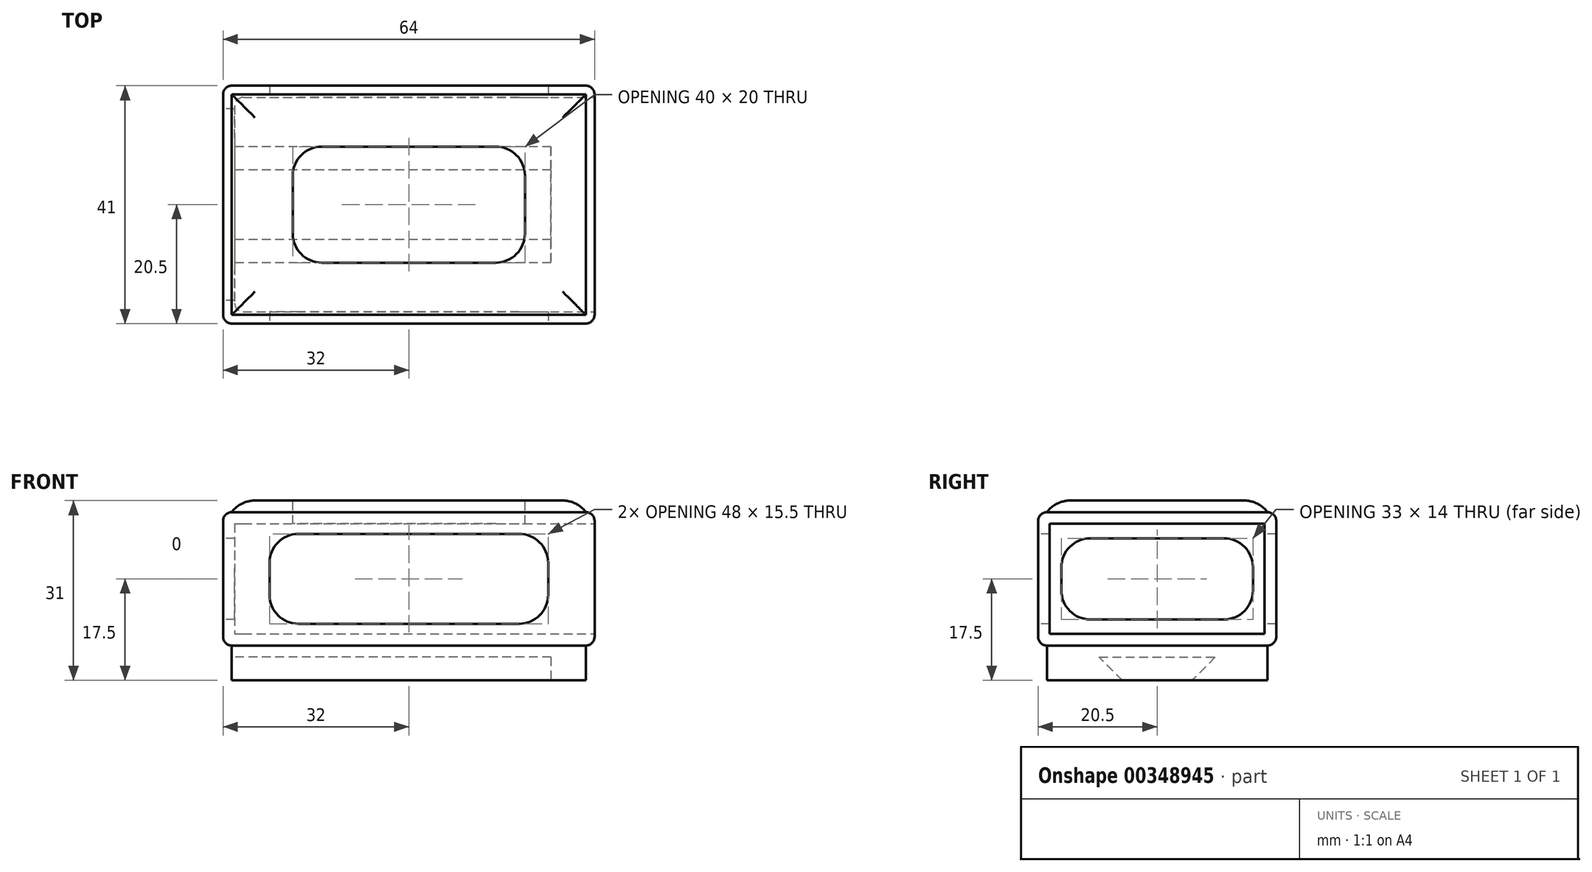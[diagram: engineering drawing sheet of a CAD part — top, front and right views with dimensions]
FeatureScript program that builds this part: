
annotation { "Feature Type Name" : "Feature", "Feature Type Description" : "" }
export const myFeature = defineFeature(function(context is Context, id is Id, definition is map)
    precondition{}
    {
        {
            var Q0;
            Q0=qCreatedBy(makeId("Top.planeOp"),FACE);
            var sketch = newSketch(context, id + "F0", { "sketchPlane" : qUnion([Q0])});
            skLineSegment(sketch, "E0.bottom", {"start": v(32, 20.5) * mm, "end": v(-32, 20.5) * mm});
            skLineSegment(sketch, "E0.top", {"start": v(32, -20.5) * mm, "end": v(-32, -20.5) * mm});
            skLineSegment(sketch, "E0.left", {"start": v(32, 20.5) * mm, "end": v(32, -20.5) * mm});
            skLineSegment(sketch, "E0.right", {"start": v(-32, 20.5) * mm, "end": v(-32, -20.5) * mm});
            skPoint(sketch, "E0.middle", {"position": v(0, 0) * mm});
            skSolve(sketch);
        }
        {
            var Q0;
            Q0=makeQuery(id+"F0.imprint","IMPRINT",FACE,{"disambiguationData":[TD([[makeQuery(id+"F0.imprint","IMPRINT",EDGE,{"derivedFrom":sQuery(id+"F0.wireOp",EDGE,"E0.bottom")}),1.0]])]});
            extrude(context, id + "F1", {"entities" : qUnion([Q0]), "depth" : 11.5 * mm});
        }
        {
            var Q0;
            Q0=makeQuery(id+"F1.opExtrude","CAP_EDGE",EDGE,{"disambiguationData":[OSD([sQuery(id+"F0.wireOp",EDGE,"E0.right")])],"isStart":false});
            var Q1;
            Q1=makeQuery(id+"F1.opExtrude","CAP_EDGE",EDGE,{"disambiguationData":[OSD([sQuery(id+"F0.wireOp",EDGE,"E0.top")])],"isStart":false});
            var Q2;
            Q2=makeQuery(id+"F1.opExtrude","CAP_EDGE",EDGE,{"disambiguationData":[OSD([sQuery(id+"F0.wireOp",EDGE,"E0.left")])],"isStart":false});
            var Q3;
            Q3=makeQuery(id+"F1.opExtrude","CAP_EDGE",EDGE,{"disambiguationData":[OSD([sQuery(id+"F0.wireOp",EDGE,"E0.bottom")])],"isStart":false});
            var Q4;
            Q4=makeQuery(id+"F1.opExtrude","SWEPT_EDGE",EDGE,{"disambiguationData":[OSD([sQuery(id+"F0.wireOp",EDGE,"E0.top"),sQuery(id+"F0.wireOp",EDGE,"E0.left")])]});
            var Q5;
            Q5=makeQuery(id+"F1.opExtrude","SWEPT_EDGE",EDGE,{"disambiguationData":[OSD([sQuery(id+"F0.wireOp",EDGE,"E0.bottom"),sQuery(id+"F0.wireOp",EDGE,"E0.left")])]});
            var Q6;
            Q6=makeQuery(id+"F1.opExtrude","SWEPT_EDGE",EDGE,{"disambiguationData":[OSD([sQuery(id+"F0.wireOp",EDGE,"E0.top"),sQuery(id+"F0.wireOp",EDGE,"E0.right")])]});
            var Q7;
            Q7=makeQuery(id+"F1.opExtrude","SWEPT_EDGE",EDGE,{"disambiguationData":[OSD([sQuery(id+"F0.wireOp",EDGE,"E0.bottom"),sQuery(id+"F0.wireOp",EDGE,"E0.right")])]});
            fillet(context, id + "F2", {"entities" : qUnion([Q0, Q1, Q2, Q3, Q4, Q5, Q6, Q7]), "radius" : 1.5 * mm, "tangentPropagation" : true, "allowEdgeOverflow" : false});
        }
        {
            var Q0;
            Q0=makeQuery(id+"F1.opExtrude","CAP_FACE",FACE,{"disambiguationData":[OSD([sQuery(id+"F0.wireOp",EDGE,"E0.bottom"),sQuery(id+"F0.wireOp",EDGE,"E0.top"),sQuery(id+"F0.wireOp",EDGE,"E0.left"),sQuery(id+"F0.wireOp",EDGE,"E0.right")])],"isStart":true});
            shell(context, id + "F3", {"entities" : qUnion([Q0]), "thickness" : 2 * mm});
        }
        {
            var Q0;
            Q0=makeQuery(id+"F3.opShell","OFFSET_EDGE",EDGE,{"disambiguationData":[OSD([sQuery(id+"F0.wireOp",EDGE,"E0.bottom"),sQuery(id+"F0.wireOp",EDGE,"E0.right")])]});
            var Q1;
            Q1=makeQuery(id+"F3.opShell","OFFSET_EDGE",EDGE,{"disambiguationData":[OSD([sQuery(id+"F0.wireOp",EDGE,"E0.top"),sQuery(id+"F0.wireOp",EDGE,"E0.right")])]});
            fillet(context, id + "F4", {"entities" : qUnion([Q0, Q1]), "radius" : 1.5 * mm, "tangentPropagation" : true, "allowEdgeOverflow" : false});
        }
        {
            var Q0;
            Q0=makeQuery(id+"F1.opExtrude","SWEPT_BODY",BODY,{"disambiguationData":[OSD([sQuery(id+"F0.wireOp",EDGE,"E0.bottom"),sQuery(id+"F0.wireOp",EDGE,"E0.top"),sQuery(id+"F0.wireOp",EDGE,"E0.left"),sQuery(id+"F0.wireOp",EDGE,"E0.right")])]});
            var Q1;
            Q1=qCreatedBy(makeId("Top.planeOp"),FACE);
            mirror(context, id + "F5", {"operationType" : NewBodyOperationType.ADD, "entities" : qUnion([Q0]), "mirrorPlane" : qUnion([Q1])});
        }
        {
            var Q0;
            {var subQ0=makeQuery(id+"F1.opExtrude","SWEPT_FACE",FACE,{"disambiguationData":[OSD([sQuery(id+"F0.wireOp",EDGE,"E0.top")])]});Q0=makeQuery(id+"F5.boolean.opBoolean","MERGE",FACE,{"derivedFrom":[subQ0,makeQuery(id+"F5.opPattern","COPY",FACE,{"derivedFrom":subQ0,"instanceName":"1"})]});}
            var sketch = newSketch(context, id + "F6", { "sketchPlane" : qUnion([Q0])});
            skLineSegment(sketch, "E1.bottom", {"start": v(24, -7.75) * mm, "end": v(-24, -7.75) * mm});
            skLineSegment(sketch, "E1.top", {"start": v(24, 7.75) * mm, "end": v(-24, 7.75) * mm});
            skLineSegment(sketch, "E1.left", {"start": v(24, -7.75) * mm, "end": v(24, 7.75) * mm});
            skLineSegment(sketch, "E1.right", {"start": v(-24, -7.75) * mm, "end": v(-24, 7.75) * mm});
            skPoint(sketch, "E1.middle", {"position": v(0, 0) * mm});
            skSolve(sketch);
        }
        {
            var Q0;
            Q0=makeQuery(id+"F6.imprint","IMPRINT",FACE,{"disambiguationData":[TD([[makeQuery(id+"F6.imprint","IMPRINT",EDGE,{"derivedFrom":sQuery(id+"F6.wireOp",EDGE,"E1.bottom")}),-1.0]])]});
            extrude(context, id + "F7", {"entities" : qUnion([Q0]), "operationType" : NewBodyOperationType.REMOVE, "endBound" : BoundingType.THROUGH_ALL, "oppositeDirection" : true, "depth" : 5 * mm});
        }
        {
            var Q0;
            {var subQ0=makeQuery(id+"F1.opExtrude","SWEPT_FACE",FACE,{"disambiguationData":[OSD([sQuery(id+"F0.wireOp",EDGE,"E0.right")])]});Q0=makeQuery(id+"F5.boolean.opBoolean","MERGE",FACE,{"derivedFrom":[subQ0,makeQuery(id+"F5.opPattern","COPY",FACE,{"derivedFrom":subQ0,"instanceName":"1"})]});}
            var sketch = newSketch(context, id + "F8", { "sketchPlane" : qUnion([Q0])});
            skLineSegment(sketch, "E2.bottom", {"start": v(16.5, 7) * mm, "end": v(-16.5, 7) * mm});
            skLineSegment(sketch, "E2.top", {"start": v(16.5, -7) * mm, "end": v(-16.5, -7) * mm});
            skLineSegment(sketch, "E2.left", {"start": v(16.5, 7) * mm, "end": v(16.5, -7) * mm});
            skLineSegment(sketch, "E2.right", {"start": v(-16.5, 7) * mm, "end": v(-16.5, -7) * mm});
            skPoint(sketch, "E2.middle", {"position": v(0, 0) * mm});
            skSolve(sketch);
        }
        {
            var Q0;
            Q0=makeQuery(id+"F8.imprint","IMPRINT",FACE,{"disambiguationData":[TD([[makeQuery(id+"F8.imprint","IMPRINT",EDGE,{"derivedFrom":sQuery(id+"F8.wireOp",EDGE,"E2.bottom")}),1.0]])]});
            extrude(context, id + "F9", {"entities" : qUnion([Q0]), "operationType" : NewBodyOperationType.REMOVE, "oppositeDirection" : true, "depth" : 5 * mm});
        }
        {
            var Q0;
            {var subQ0=sQuery(id+"F0.wireOp",EDGE,"E0.left");var subQ2=makeQuery(id+"F1.opExtrude","SWEPT_FACE",FACE,{"disambiguationData":[OSD([subQ0])]});var subQ3=sQuery(id+"F8.wireOp",EDGE,"E2.right");var subQ4=sQuery(id+"F8.wireOp",EDGE,"E2.top");Q0=makeQuery(id+"F9.boolean.opBoolean","COPY",EDGE,{"disambiguationData":[TD([subQ2])],"derivedFrom":makeQuery(id+"F9.opExtrude","SWEPT_EDGE",EDGE,{"disambiguationData":[OSD([subQ4,subQ3])]})});}
            var Q1;
            {var subQ0=sQuery(id+"F0.wireOp",EDGE,"E0.right");var subQ2=makeQuery(id+"F1.opExtrude","SWEPT_FACE",FACE,{"disambiguationData":[OSD([subQ0])]});var subQ3=sQuery(id+"F8.wireOp",EDGE,"E2.top");var subQ4=sQuery(id+"F8.wireOp",EDGE,"E2.right");Q1=makeQuery(id+"F9.boolean.opBoolean","COPY",EDGE,{"disambiguationData":[TD([subQ2])],"derivedFrom":makeQuery(id+"F9.opExtrude","SWEPT_EDGE",EDGE,{"disambiguationData":[OSD([subQ3,subQ4])]})});}
            var Q2;
            {var subQ0=sQuery(id+"F0.wireOp",EDGE,"E0.left");var subQ2=makeQuery(id+"F1.opExtrude","SWEPT_FACE",FACE,{"disambiguationData":[OSD([subQ0])]});var subQ3=sQuery(id+"F8.wireOp",EDGE,"E2.top");var subQ4=sQuery(id+"F8.wireOp",EDGE,"E2.left");Q2=makeQuery(id+"F9.boolean.opBoolean","COPY",EDGE,{"disambiguationData":[TD([subQ2])],"derivedFrom":makeQuery(id+"F9.opExtrude","SWEPT_EDGE",EDGE,{"disambiguationData":[OSD([subQ3,subQ4])]})});}
            var Q3;
            {var subQ0=sQuery(id+"F0.wireOp",EDGE,"E0.right");var subQ2=makeQuery(id+"F1.opExtrude","SWEPT_FACE",FACE,{"disambiguationData":[OSD([subQ0])]});var subQ3=sQuery(id+"F8.wireOp",EDGE,"E2.top");var subQ4=sQuery(id+"F8.wireOp",EDGE,"E2.left");Q3=makeQuery(id+"F9.boolean.opBoolean","COPY",EDGE,{"disambiguationData":[TD([subQ2])],"derivedFrom":makeQuery(id+"F9.opExtrude","SWEPT_EDGE",EDGE,{"disambiguationData":[OSD([subQ3,subQ4])]})});}
            var Q4;
            {var subQ0=sQuery(id+"F0.wireOp",EDGE,"E0.left");var subQ2=makeQuery(id+"F1.opExtrude","SWEPT_FACE",FACE,{"disambiguationData":[OSD([subQ0])]});var subQ3=sQuery(id+"F8.wireOp",EDGE,"E2.right");var subQ4=sQuery(id+"F8.wireOp",EDGE,"E2.bottom");Q4=makeQuery(id+"F9.boolean.opBoolean","COPY",EDGE,{"disambiguationData":[TD([subQ2])],"derivedFrom":makeQuery(id+"F9.opExtrude","SWEPT_EDGE",EDGE,{"disambiguationData":[OSD([subQ4,subQ3])]})});}
            var Q5;
            {var subQ0=sQuery(id+"F0.wireOp",EDGE,"E0.right");var subQ2=makeQuery(id+"F1.opExtrude","SWEPT_FACE",FACE,{"disambiguationData":[OSD([subQ0])]});var subQ3=sQuery(id+"F8.wireOp",EDGE,"E2.bottom");var subQ4=sQuery(id+"F8.wireOp",EDGE,"E2.right");Q5=makeQuery(id+"F9.boolean.opBoolean","COPY",EDGE,{"disambiguationData":[TD([subQ2])],"derivedFrom":makeQuery(id+"F9.opExtrude","SWEPT_EDGE",EDGE,{"disambiguationData":[OSD([subQ3,subQ4])]})});}
            var Q6;
            {var subQ0=sQuery(id+"F0.wireOp",EDGE,"E0.right");var subQ2=sQuery(id+"F8.wireOp",EDGE,"E2.bottom");var subQ3=makeQuery(id+"F1.opExtrude","SWEPT_FACE",FACE,{"disambiguationData":[OSD([subQ0])]});var subQ4=sQuery(id+"F8.wireOp",EDGE,"E2.left");Q6=makeQuery(id+"F9.boolean.opBoolean","COPY",EDGE,{"disambiguationData":[TD([subQ3])],"derivedFrom":makeQuery(id+"F9.opExtrude","SWEPT_EDGE",EDGE,{"disambiguationData":[OSD([subQ2,subQ4])]})});}
            var Q7;
            {var subQ0=sQuery(id+"F0.wireOp",EDGE,"E0.left");var subQ2=makeQuery(id+"F1.opExtrude","SWEPT_FACE",FACE,{"disambiguationData":[OSD([subQ0])]});var subQ3=sQuery(id+"F8.wireOp",EDGE,"E2.bottom");var subQ4=sQuery(id+"F8.wireOp",EDGE,"E2.left");Q7=makeQuery(id+"F9.boolean.opBoolean","COPY",EDGE,{"disambiguationData":[TD([subQ2])],"derivedFrom":makeQuery(id+"F9.opExtrude","SWEPT_EDGE",EDGE,{"disambiguationData":[OSD([subQ3,subQ4])]})});}
            fillet(context, id + "F10", {"entities" : qUnion([Q0, Q1, Q2, Q3, Q4, Q5, Q6, Q7]), "radius" : 5 * mm, "tangentPropagation" : true, "allowEdgeOverflow" : false});
        }
        {
            var Q0;
            {var subQ0=sQuery(id+"F0.wireOp",EDGE,"E0.top");var subQ2=makeQuery(id+"F1.opExtrude","SWEPT_FACE",FACE,{"disambiguationData":[OSD([subQ0])]});var subQ3=sQuery(id+"F6.wireOp",EDGE,"E1.top");var subQ4=sQuery(id+"F6.wireOp",EDGE,"E1.right");Q0=makeQuery(id+"F7.boolean.opBoolean","COPY",EDGE,{"disambiguationData":[TD([subQ2])],"derivedFrom":makeQuery(id+"F7.opExtrude","SWEPT_EDGE",EDGE,{"disambiguationData":[OSD([subQ3,subQ4])]})});}
            var Q1;
            {var subQ0=sQuery(id+"F0.wireOp",EDGE,"E0.top");var subQ2=makeQuery(id+"F1.opExtrude","SWEPT_FACE",FACE,{"disambiguationData":[OSD([subQ0])]});var subQ3=sQuery(id+"F6.wireOp",EDGE,"E1.left");var subQ4=sQuery(id+"F6.wireOp",EDGE,"E1.top");Q1=makeQuery(id+"F7.boolean.opBoolean","COPY",EDGE,{"disambiguationData":[TD([subQ2])],"derivedFrom":makeQuery(id+"F7.opExtrude","SWEPT_EDGE",EDGE,{"disambiguationData":[OSD([subQ4,subQ3])]})});}
            var Q2;
            {var subQ0=sQuery(id+"F0.wireOp",EDGE,"E0.top");var subQ2=sQuery(id+"F6.wireOp",EDGE,"E1.bottom");var subQ3=makeQuery(id+"F1.opExtrude","SWEPT_FACE",FACE,{"disambiguationData":[OSD([subQ0])]});var subQ4=sQuery(id+"F6.wireOp",EDGE,"E1.right");Q2=makeQuery(id+"F7.boolean.opBoolean","COPY",EDGE,{"disambiguationData":[TD([subQ3])],"derivedFrom":makeQuery(id+"F7.opExtrude","SWEPT_EDGE",EDGE,{"disambiguationData":[OSD([subQ2,subQ4])]})});}
            var Q3;
            {var subQ0=sQuery(id+"F0.wireOp",EDGE,"E0.top");var subQ2=sQuery(id+"F6.wireOp",EDGE,"E1.bottom");var subQ3=makeQuery(id+"F1.opExtrude","SWEPT_FACE",FACE,{"disambiguationData":[OSD([subQ0])]});var subQ4=sQuery(id+"F6.wireOp",EDGE,"E1.left");Q3=makeQuery(id+"F7.boolean.opBoolean","COPY",EDGE,{"disambiguationData":[TD([subQ3])],"derivedFrom":makeQuery(id+"F7.opExtrude","SWEPT_EDGE",EDGE,{"disambiguationData":[OSD([subQ2,subQ4])]})});}
            fillet(context, id + "F11", {"entities" : qUnion([Q0, Q1, Q2, Q3]), "radius" : 5 * mm, "tangentPropagation" : true, "allowEdgeOverflow" : false});
        }
        {
            var Q0;
            {var subQ0=sQuery(id+"F0.wireOp",EDGE,"E0.bottom");var subQ1=makeQuery(id+"F1.opExtrude","SWEPT_FACE",FACE,{"disambiguationData":[OSD([subQ0])]});var subQ3=sQuery(id+"F6.wireOp",EDGE,"E1.top");var subQ4=sQuery(id+"F6.wireOp",EDGE,"E1.left");Q0=makeQuery(id+"F7.boolean.opBoolean","COPY",EDGE,{"disambiguationData":[TD([subQ1])],"derivedFrom":makeQuery(id+"F7.opExtrude","SWEPT_EDGE",EDGE,{"disambiguationData":[OSD([subQ3,subQ4])]})});}
            var Q1;
            {var subQ0=sQuery(id+"F0.wireOp",EDGE,"E0.bottom");var subQ1=makeQuery(id+"F1.opExtrude","SWEPT_FACE",FACE,{"disambiguationData":[OSD([subQ0])]});var subQ3=sQuery(id+"F6.wireOp",EDGE,"E1.bottom");var subQ4=sQuery(id+"F6.wireOp",EDGE,"E1.left");Q1=makeQuery(id+"F7.boolean.opBoolean","COPY",EDGE,{"disambiguationData":[TD([subQ1])],"derivedFrom":makeQuery(id+"F7.opExtrude","SWEPT_EDGE",EDGE,{"disambiguationData":[OSD([subQ3,subQ4])]})});}
            var Q2;
            {var subQ0=sQuery(id+"F0.wireOp",EDGE,"E0.bottom");var subQ1=makeQuery(id+"F1.opExtrude","SWEPT_FACE",FACE,{"disambiguationData":[OSD([subQ0])]});var subQ3=sQuery(id+"F6.wireOp",EDGE,"E1.right");var subQ4=sQuery(id+"F6.wireOp",EDGE,"E1.bottom");Q2=makeQuery(id+"F7.boolean.opBoolean","COPY",EDGE,{"disambiguationData":[TD([subQ1])],"derivedFrom":makeQuery(id+"F7.opExtrude","SWEPT_EDGE",EDGE,{"disambiguationData":[OSD([subQ4,subQ3])]})});}
            var Q3;
            {var subQ0=sQuery(id+"F0.wireOp",EDGE,"E0.bottom");var subQ1=makeQuery(id+"F1.opExtrude","SWEPT_FACE",FACE,{"disambiguationData":[OSD([subQ0])]});var subQ3=sQuery(id+"F6.wireOp",EDGE,"E1.right");var subQ4=sQuery(id+"F6.wireOp",EDGE,"E1.top");Q3=makeQuery(id+"F7.boolean.opBoolean","COPY",EDGE,{"disambiguationData":[TD([subQ1])],"derivedFrom":makeQuery(id+"F7.opExtrude","SWEPT_EDGE",EDGE,{"disambiguationData":[OSD([subQ4,subQ3])]})});}
            fillet(context, id + "F12", {"entities" : qUnion([Q0, Q1, Q2, Q3]), "radius" : 5 * mm, "tangentPropagation" : true, "allowEdgeOverflow" : false});
        }
        {
            var Q0;
            Q0=makeQuery(id+"F1.opExtrude","CAP_FACE",FACE,{"disambiguationData":[OSD([sQuery(id+"F0.wireOp",EDGE,"E0.bottom"),sQuery(id+"F0.wireOp",EDGE,"E0.top"),sQuery(id+"F0.wireOp",EDGE,"E0.left"),sQuery(id+"F0.wireOp",EDGE,"E0.right")])],"isStart":false});
            var sketch = newSketch(context, id + "F13", { "sketchPlane" : qUnion([Q0])});
            skLineSegment(sketch, "E3.bottom", {"start": v(20, -10) * mm, "end": v(-20, -10) * mm});
            skLineSegment(sketch, "E3.top", {"start": v(20, 10) * mm, "end": v(-20, 10) * mm});
            skLineSegment(sketch, "E3.left", {"start": v(20, -10) * mm, "end": v(20, 10) * mm});
            skLineSegment(sketch, "E3.right", {"start": v(-20, -10) * mm, "end": v(-20, 10) * mm});
            skPoint(sketch, "E3.middle", {"position": v(0, 0) * mm});
            skSolve(sketch);
        }
        {
            var Q0;
            Q0=makeQuery(id+"F13.imprint","IMPRINT",FACE,{"disambiguationData":[TD([[makeQuery(id+"F13.imprint","IMPRINT",EDGE,{"derivedFrom":sQuery(id+"F13.wireOp",EDGE,"E3.bottom")}),-1.0]])]});
            extrude(context, id + "F14", {"entities" : qUnion([Q0]), "operationType" : NewBodyOperationType.REMOVE, "oppositeDirection" : true, "depth" : 5 * mm});
        }
        {
            var Q0;
            Q0=makeQuery(id+"F14.boolean.opBoolean","COPY",EDGE,{"derivedFrom":makeQuery(id+"F14.opExtrude","SWEPT_EDGE",EDGE,{"disambiguationData":[OSD([sQuery(id+"F13.wireOp",EDGE,"E3.top"),sQuery(id+"F13.wireOp",EDGE,"E3.right")])]})});
            var Q1;
            Q1=makeQuery(id+"F14.boolean.opBoolean","COPY",EDGE,{"derivedFrom":makeQuery(id+"F14.opExtrude","SWEPT_EDGE",EDGE,{"disambiguationData":[OSD([sQuery(id+"F13.wireOp",EDGE,"E3.bottom"),sQuery(id+"F13.wireOp",EDGE,"E3.right")])]})});
            var Q2;
            Q2=makeQuery(id+"F14.boolean.opBoolean","COPY",EDGE,{"derivedFrom":makeQuery(id+"F14.opExtrude","SWEPT_EDGE",EDGE,{"disambiguationData":[OSD([sQuery(id+"F13.wireOp",EDGE,"E3.bottom"),sQuery(id+"F13.wireOp",EDGE,"E3.left")])]})});
            var Q3;
            Q3=makeQuery(id+"F14.boolean.opBoolean","COPY",EDGE,{"derivedFrom":makeQuery(id+"F14.opExtrude","SWEPT_EDGE",EDGE,{"disambiguationData":[OSD([sQuery(id+"F13.wireOp",EDGE,"E3.top"),sQuery(id+"F13.wireOp",EDGE,"E3.left")])]})});
            fillet(context, id + "F15", {"entities" : qUnion([Q0, Q1, Q2, Q3]), "radius" : 5 * mm, "tangentPropagation" : true, "allowEdgeOverflow" : false});
        }
        {
            var Q0;
            {var subQ0=makeQuery(id+"F1.opExtrude","SWEPT_FACE",FACE,{"disambiguationData":[OSD([sQuery(id+"F0.wireOp",EDGE,"E0.left")])]});Q0=makeQuery(id+"F5.boolean.opBoolean","MERGE",FACE,{"derivedFrom":[subQ0,makeQuery(id+"F5.opPattern","COPY",FACE,{"derivedFrom":subQ0,"instanceName":"1"})]});}
            var sketch = newSketch(context, id + "F16", { "sketchPlane" : qUnion([Q0])});
            skLineSegment(sketch, "E4.bottom", {"start": v(18.5, -9.5) * mm, "end": v(-18.5, -9.5) * mm});
            skLineSegment(sketch, "E4.top", {"start": v(18.5, 9.5) * mm, "end": v(-18.5, 9.5) * mm});
            skLineSegment(sketch, "E4.left", {"start": v(18.5, -9.5) * mm, "end": v(18.5, 9.5) * mm});
            skLineSegment(sketch, "E4.right", {"start": v(-18.5, -9.5) * mm, "end": v(-18.5, 9.5) * mm});
            skPoint(sketch, "E4.middle", {"position": v(0, 0) * mm});
            skSolve(sketch);
        }
        {
            var Q0;
            Q0=makeQuery(id+"F16.imprint","IMPRINT",FACE,{"disambiguationData":[TD([[makeQuery(id+"F16.imprint","IMPRINT",EDGE,{"derivedFrom":sQuery(id+"F16.wireOp",EDGE,"E4.bottom")}),-1.0]])]});
            extrude(context, id + "F17", {"entities" : qUnion([Q0]), "operationType" : NewBodyOperationType.REMOVE, "oppositeDirection" : true, "depth" : 5 * mm});
        }
        {
            var Q0;
            Q0=makeQuery(id+"F5.opPattern","COPY",FACE,{"derivedFrom":makeQuery(id+"F1.opExtrude","CAP_FACE",FACE,{"disambiguationData":[OSD([sQuery(id+"F0.wireOp",EDGE,"E0.bottom"),sQuery(id+"F0.wireOp",EDGE,"E0.top"),sQuery(id+"F0.wireOp",EDGE,"E0.left"),sQuery(id+"F0.wireOp",EDGE,"E0.right")])],"isStart":false}),"instanceName":"1"});
            var sketch = newSketch(context, id + "F18", { "sketchPlane" : qUnion([Q0])});
            skLineSegment(sketch, "E5.bottom", {"start": v(30.5, -19) * mm, "end": v(-30.5, -19) * mm});
            skLineSegment(sketch, "E5.top", {"start": v(30.5, 19) * mm, "end": v(-30.5, 19) * mm});
            skLineSegment(sketch, "E5.left", {"start": v(30.5, -19) * mm, "end": v(30.5, 19) * mm});
            skLineSegment(sketch, "E5.right", {"start": v(-30.5, -19) * mm, "end": v(-30.5, 19) * mm});
            skPoint(sketch, "E5.middle", {"position": v(0, 0) * mm});
            skSolve(sketch);
        }
        {
            var Q0;
            Q0=makeQuery(id+"F18.imprint","IMPRINT",FACE,{"disambiguationData":[TD([[makeQuery(id+"F18.imprint","IMPRINT",EDGE,{"derivedFrom":sQuery(id+"F18.wireOp",EDGE,"E5.bottom")}),-1.0]])]});
            extrude(context, id + "F19", {"entities" : qUnion([Q0]), "operationType" : NewBodyOperationType.ADD, "depth" : 6 * mm});
        }
        {
            var Q0;
            Q0=makeQuery(id+"F19.opExtrude","SWEPT_FACE",FACE,{"disambiguationData":[OSD([sQuery(id+"F18.wireOp",EDGE,"E5.right")])]});
            var sketch = newSketch(context, id + "F20", { "sketchPlane" : qUnion([Q0])});
            skLineSegment(sketch, "E6.bottom", {"start": v(10, -21.5) * mm, "end": v(-10, -21.5) * mm, "construction": true});
            skLineSegment(sketch, "E6.top", {"start": v(10, -13.5) * mm, "end": v(-10, -13.5) * mm, "construction": true});
            skLineSegment(sketch, "E6.left", {"start": v(10, -21.5) * mm, "end": v(10, -13.5) * mm, "construction": true});
            skLineSegment(sketch, "E6.right", {"start": v(-10, -21.5) * mm, "end": v(-10, -13.5) * mm, "construction": true});
            skPoint(sketch, "E6.middle", {"position": v(0, -17.5) * mm});
            skLineSegment(sketch, "E7.bottom", {"start": v(6, -21.5) * mm, "end": v(-6, -21.5) * mm, "construction": true});
            skLineSegment(sketch, "E7.top", {"start": v(6, -13.5) * mm, "end": v(-6, -13.5) * mm, "construction": true});
            skLineSegment(sketch, "E7.left", {"start": v(6, -21.5) * mm, "end": v(6, -13.5) * mm, "construction": true});
            skLineSegment(sketch, "E7.right", {"start": v(-6, -21.5) * mm, "end": v(-6, -13.5) * mm, "construction": true});
            skPoint(sketch, "E8", {"position": v(-6, -17.5) * mm});
            skPoint(sketch, "E9", {"position": v(6, -17.5) * mm});
            skLineSegment(sketch, "E10", {"start": v(6, -17.5) * mm, "end": v(-6, -17.5) * mm, "construction": true});
            skLineSegment(sketch, "E11", {"start": v(6, -17.5) * mm, "end": v(-6, -17.5) * mm});
            skLineSegment(sketch, "E12", {"start": v(-10, -13.5) * mm, "end": v(-6, -17.5) * mm});
            skLineSegment(sketch, "E13", {"start": v(6, -17.5) * mm, "end": v(10, -13.5) * mm});
            skLineSegment(sketch, "E14", {"start": v(10, -13.5) * mm, "end": v(-10, -13.5) * mm});
            skSolve(sketch);
        }
        {
            var Q0;
            Q0=makeQuery(id+"F20.imprint","IMPRINT",FACE,{"disambiguationData":[TD([[makeQuery(id+"F20.imprint","IMPRINT",EDGE,{"derivedFrom":sQuery(id+"F20.wireOp",EDGE,"E11")}),1.0]])]});
            extrude(context, id + "F21", {"entities" : qUnion([Q0]), "operationType" : NewBodyOperationType.REMOVE, "oppositeDirection" : true, "depth" : 55 * mm});
        }
        {
            var Q0;
            Q0=makeQuery(id+"F1.opExtrude","CAP_FACE",FACE,{"disambiguationData":[OSD([sQuery(id+"F0.wireOp",EDGE,"E0.bottom"),sQuery(id+"F0.wireOp",EDGE,"E0.top"),sQuery(id+"F0.wireOp",EDGE,"E0.left"),sQuery(id+"F0.wireOp",EDGE,"E0.right")])],"isStart":false});
            extrude(context, id + "F22", {"entities" : qUnion([Q0]), "operationType" : NewBodyOperationType.ADD, "depth" : 2 * mm});
        }
        {
            var Q0;
            {var subQ0=sQuery(id+"F0.wireOp",EDGE,"E0.right");var subQ1=sQuery(id+"F0.wireOp",EDGE,"E0.left");var subQ2=sQuery(id+"F0.wireOp",EDGE,"E0.top");var subQ3=sQuery(id+"F0.wireOp",EDGE,"E0.bottom");Q0=makeQuery(id+"F22.opExtrude","CAP_EDGE",EDGE,{"disambiguationData":[OSD([subQ3,subQ2,subQ1,subQ0]),TDD([makeQuery(id+"F2.opFillet","BLEND_EDGE",EDGE,{"blendedFrom":[makeQuery(id+"F1.opExtrude","CAP_EDGE",EDGE,{"disambiguationData":[OSD([subQ2])],"isStart":false}),makeQuery(id+"F1.opExtrude","CAP_FACE",FACE,{"disambiguationData":[OSD([subQ3,subQ2,subQ1,subQ0])],"isStart":false})],"blendedInto":[makeQuery(id+"F1.opExtrude","CAP_FACE",FACE,{"disambiguationData":[OSD([subQ3,subQ2,subQ1,subQ0])],"isStart":false})]})])],"isStart":false});}
            var Q1;
            {var subQ0=sQuery(id+"F0.wireOp",EDGE,"E0.right");var subQ1=sQuery(id+"F0.wireOp",EDGE,"E0.left");var subQ2=sQuery(id+"F0.wireOp",EDGE,"E0.top");var subQ3=sQuery(id+"F0.wireOp",EDGE,"E0.bottom");Q1=makeQuery(id+"F22.opExtrude","CAP_EDGE",EDGE,{"disambiguationData":[OSD([subQ3,subQ2,subQ1,subQ0]),TDD([makeQuery(id+"F2.opFillet","BLEND_EDGE",EDGE,{"blendedFrom":[makeQuery(id+"F1.opExtrude","CAP_EDGE",EDGE,{"disambiguationData":[OSD([subQ1])],"isStart":false}),makeQuery(id+"F1.opExtrude","CAP_FACE",FACE,{"disambiguationData":[OSD([subQ3,subQ2,subQ1,subQ0])],"isStart":false})],"blendedInto":[makeQuery(id+"F1.opExtrude","CAP_FACE",FACE,{"disambiguationData":[OSD([subQ3,subQ2,subQ1,subQ0])],"isStart":false})]})])],"isStart":false});}
            var Q2;
            {var subQ0=sQuery(id+"F0.wireOp",EDGE,"E0.right");var subQ1=sQuery(id+"F0.wireOp",EDGE,"E0.left");var subQ2=sQuery(id+"F0.wireOp",EDGE,"E0.top");var subQ3=sQuery(id+"F0.wireOp",EDGE,"E0.bottom");Q2=makeQuery(id+"F22.opExtrude","CAP_EDGE",EDGE,{"disambiguationData":[OSD([subQ3,subQ2,subQ1,subQ0]),TDD([makeQuery(id+"F2.opFillet","BLEND_EDGE",EDGE,{"blendedFrom":[makeQuery(id+"F1.opExtrude","CAP_EDGE",EDGE,{"disambiguationData":[OSD([subQ0])],"isStart":false}),makeQuery(id+"F1.opExtrude","CAP_FACE",FACE,{"disambiguationData":[OSD([subQ3,subQ2,subQ1,subQ0])],"isStart":false})],"blendedInto":[makeQuery(id+"F1.opExtrude","CAP_FACE",FACE,{"disambiguationData":[OSD([subQ3,subQ2,subQ1,subQ0])],"isStart":false})]})])],"isStart":false});}
            var Q3;
            {var subQ0=sQuery(id+"F0.wireOp",EDGE,"E0.right");var subQ1=sQuery(id+"F0.wireOp",EDGE,"E0.left");var subQ2=sQuery(id+"F0.wireOp",EDGE,"E0.top");var subQ3=sQuery(id+"F0.wireOp",EDGE,"E0.bottom");Q3=makeQuery(id+"F22.opExtrude","CAP_EDGE",EDGE,{"disambiguationData":[OSD([subQ3,subQ2,subQ1,subQ0]),TDD([makeQuery(id+"F2.opFillet","BLEND_EDGE",EDGE,{"blendedFrom":[makeQuery(id+"F1.opExtrude","CAP_EDGE",EDGE,{"disambiguationData":[OSD([subQ3])],"isStart":false}),makeQuery(id+"F1.opExtrude","CAP_FACE",FACE,{"disambiguationData":[OSD([subQ3,subQ2,subQ1,subQ0])],"isStart":false})],"blendedInto":[makeQuery(id+"F1.opExtrude","CAP_FACE",FACE,{"disambiguationData":[OSD([subQ3,subQ2,subQ1,subQ0])],"isStart":false})]})])],"isStart":false});}
            fillet(context, id + "F23", {"entities" : qUnion([Q0, Q1, Q2, Q3]), "radius" : 5 * mm, "tangentPropagation" : true, "allowEdgeOverflow" : false});
        }
    });
